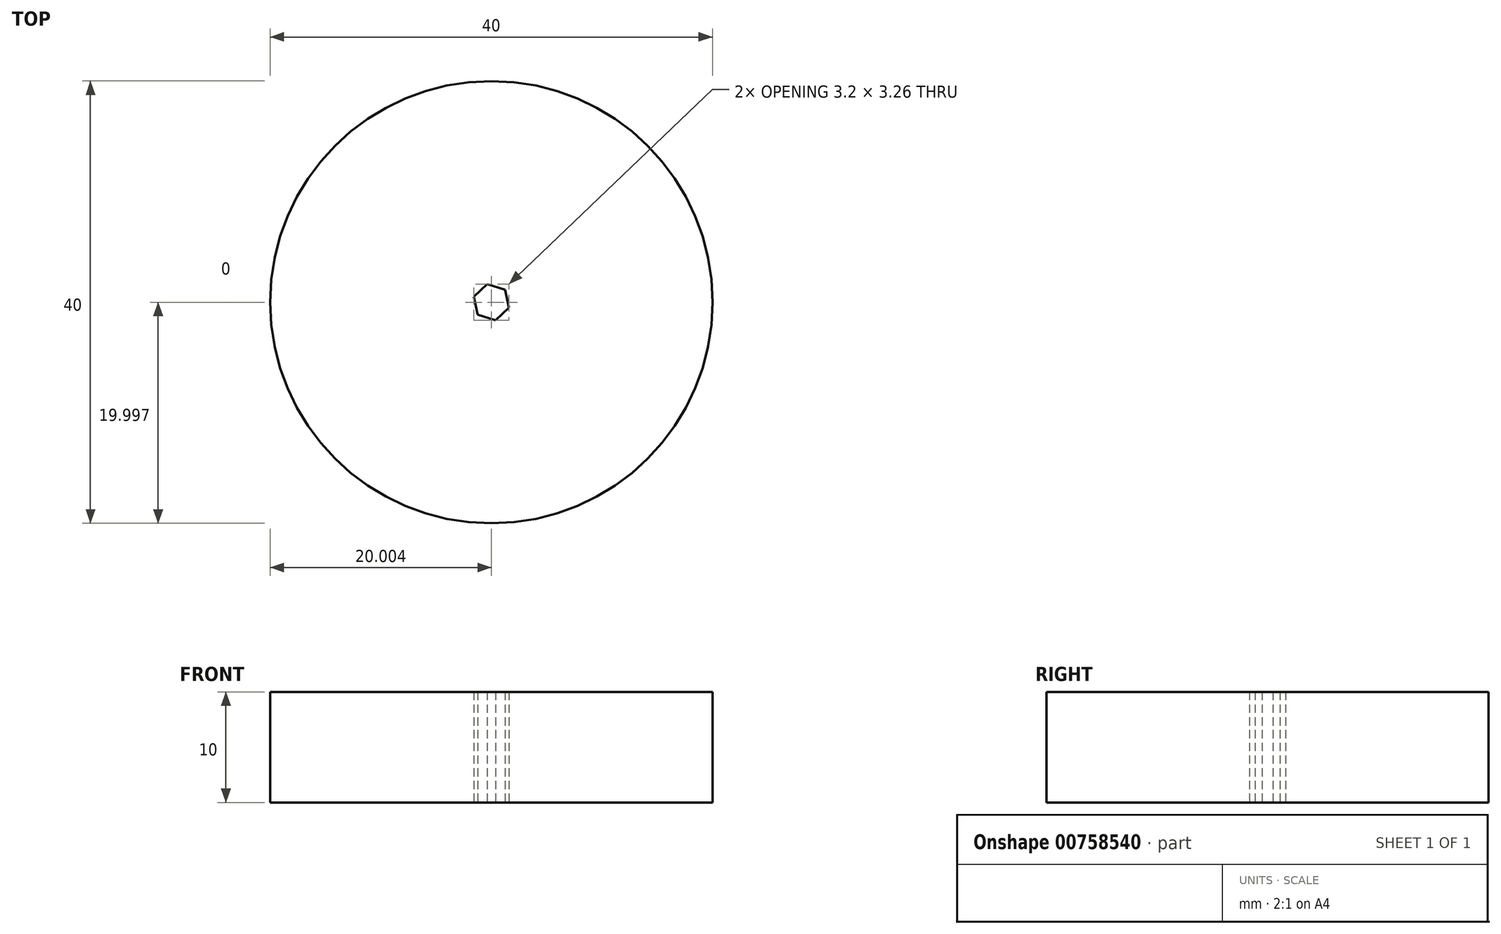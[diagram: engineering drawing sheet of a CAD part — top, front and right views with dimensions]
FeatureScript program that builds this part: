
annotation { "Feature Type Name" : "Feature", "Feature Type Description" : "" }
export const myFeature = defineFeature(function(context is Context, id is Id, definition is map)
    precondition{}
    {
        {
            var Q0;
            Q0=qCreatedBy(makeId("Top.planeOp"),FACE);
            var sketch = newSketch(context, id + "F0", { "sketchPlane" : qUnion([Q0])});
            skCircle(sketch, "E0", {"center": v(31.9, 28.43) * mm, "radius": 20 * mm});
            skCircle(sketch, "E1.cCircle", {"center": v(31.9, 28.43) * mm, "radius": 1.45 * mm, "construction": true});
            skLineSegment(sketch, "E1.0", {"start": v(33.5, 27.93) * mm, "end": v(32.28, 26.8) * mm});
            skLineSegment(sketch, "E1.1", {"start": v(32.28, 26.8) * mm, "end": v(30.68, 27.29) * mm});
            skLineSegment(sketch, "E1.2", {"start": v(30.68, 27.29) * mm, "end": v(30.3, 28.92) * mm});
            skLineSegment(sketch, "E1.3", {"start": v(30.3, 28.92) * mm, "end": v(31.53, 30.06) * mm});
            skLineSegment(sketch, "E1.4", {"start": v(31.53, 30.06) * mm, "end": v(33.13, 29.57) * mm});
            skLineSegment(sketch, "E1.5", {"start": v(33.13, 29.57) * mm, "end": v(33.5, 27.93) * mm});
            skPoint(sketch, "E1.0.midPoint", {"position": v(32.9, 27.37) * mm});
            skSolve(sketch);
        }
        {
            var Q0;
            Q0=makeQuery(id+"F0.imprint","IMPRINT",FACE,{"disambiguationData":[TD([[makeQuery(id+"F0.imprint","IMPRINT",EDGE,{"derivedFrom":sQuery(id+"F0.wireOp",EDGE,"E0")}),1.0]])]});
            extrude(context, id + "F1", {"entities" : qUnion([Q0]), "depth" : 10 * mm, "offsetDistance" : 25 * mm});
        }
        {
            var Q0;
            Q0=makeQuery(id+"F0.imprint","IMPRINT",FACE,{"disambiguationData":[TD([[makeQuery(id+"F0.imprint","IMPRINT",EDGE,{"derivedFrom":sQuery(id+"F0.wireOp",EDGE,"BqwUMK7o-UOgA-bkrt-Crtr-ZBT60VQhf2Sd")}),1.0]])]});
            var Q1;
            Q1=makeQuery(id+"F0.imprint","IMPRINT",FACE,{"disambiguationData":[TD([[makeQuery(id+"F0.imprint","IMPRINT",EDGE,{"derivedFrom":sQuery(id+"F0.wireOp",EDGE,"E0")}),1.0]])]});
            extrude(context, id + "F2", {"entities" : qUnion([Q0, Q1]), "depth" : 10 * mm, "offsetDistance" : 25.4 * mm});
        }
    });
